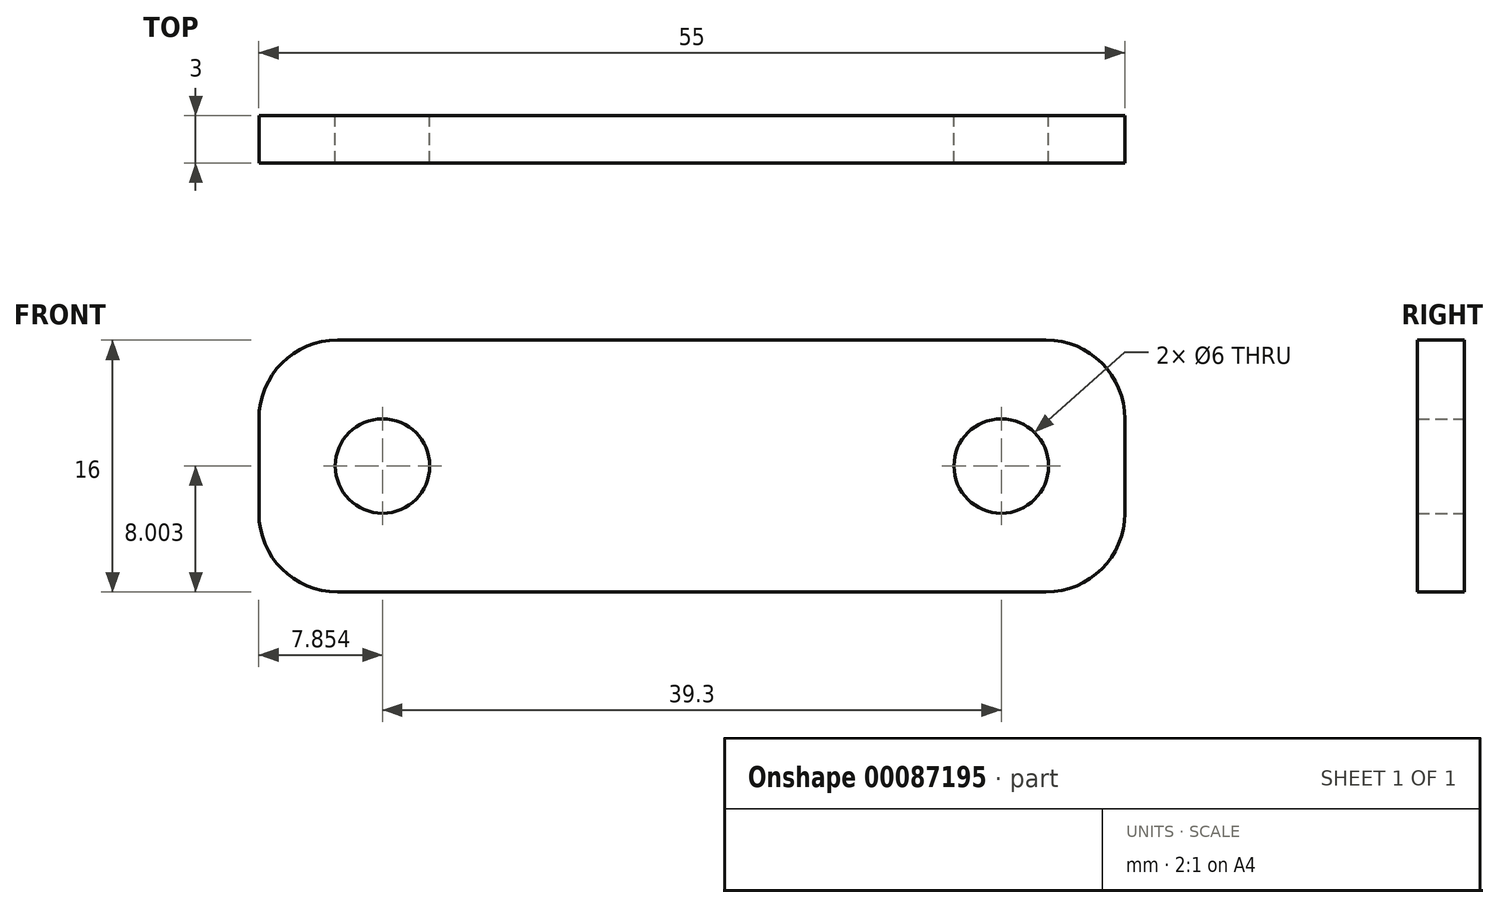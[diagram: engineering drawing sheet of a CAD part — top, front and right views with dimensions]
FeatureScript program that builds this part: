
annotation { "Feature Type Name" : "Feature", "Feature Type Description" : "" }
export const myFeature = defineFeature(function(context is Context, id is Id, definition is map)
    precondition{}
    {
        {
            var Q0;
            Q0=qCreatedBy(makeId("Front.planeOp"),FACE);
            var sketch = newSketch(context, id + "F0", { "sketchPlane" : qUnion([Q0])});
            skLineSegment(sketch, "E0", {"start": v(-167.59, 33.38) * mm, "end": v(-128.29, 33.38) * mm, "construction": true});
            skCircle(sketch, "E1", {"center": v(-167.59, 33.38) * mm, "radius": 3 * mm});
            skCircle(sketch, "E2", {"center": v(-128.29, 33.38) * mm, "radius": 3 * mm});
            skLineSegment(sketch, "E3.bottom", {"start": v(-125.44, 41.38) * mm, "end": v(-170.44, 41.38) * mm});
            skLineSegment(sketch, "E3.top", {"start": v(-125.44, 25.38) * mm, "end": v(-170.44, 25.38) * mm});
            skLineSegment(sketch, "E3.left", {"start": v(-120.44, 36.38) * mm, "end": v(-120.44, 30.38) * mm});
            skLineSegment(sketch, "E3.right", {"start": v(-175.44, 36.38) * mm, "end": v(-175.44, 30.38) * mm});
            skPoint(sketch, "E3.middle", {"position": v(-147.94, 33.38) * mm});
            skPoint(sketch, "E4.visualSharp", {"position": v(-120.44, 41.38) * mm});
            skArc(sketch, "E4.filletArc", {"start": v(-120.44, 36.38) * mm, "mid": v(-121.9, 39.92) * mm, "end": v(-125.44, 41.38) * mm});
            skPoint(sketch, "E5.visualSharp", {"position": v(-120.44, 25.38) * mm});
            skArc(sketch, "E5.filletArc", {"start": v(-125.44, 25.38) * mm, "mid": v(-121.9, 26.85) * mm, "end": v(-120.44, 30.38) * mm});
            skPoint(sketch, "E6.visualSharp", {"position": v(-175.44, 25.38) * mm});
            skArc(sketch, "E6.filletArc", {"start": v(-175.44, 30.38) * mm, "mid": v(-173.97, 26.85) * mm, "end": v(-170.44, 25.38) * mm});
            skPoint(sketch, "E7.visualSharp", {"position": v(-175.44, 41.38) * mm});
            skArc(sketch, "E7.filletArc", {"start": v(-170.44, 41.38) * mm, "mid": v(-173.97, 39.92) * mm, "end": v(-175.44, 36.38) * mm});
            skSolve(sketch);
        }
        {
            var Q0;
            Q0=qSketchRegion(id+"F0",true);
            extrude(context, id + "F1", {"entities" : qUnion([Q0]), "depth" : 3 * mm});
        }
    });
